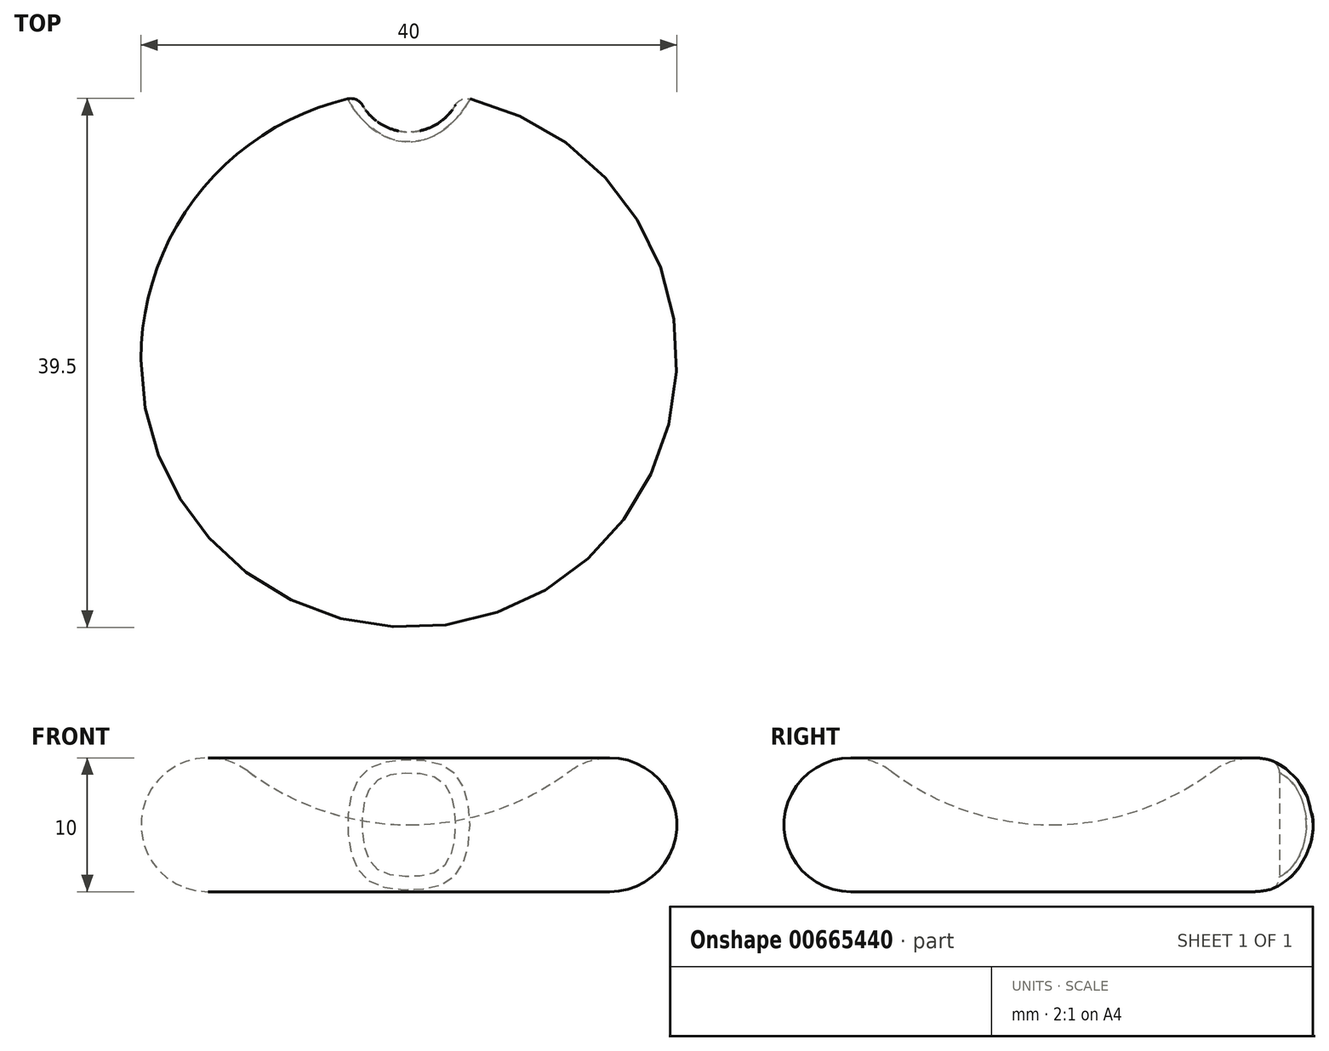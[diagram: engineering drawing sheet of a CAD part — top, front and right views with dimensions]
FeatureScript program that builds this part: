
annotation { "Feature Type Name" : "Feature", "Feature Type Description" : "" }
export const myFeature = defineFeature(function(context is Context, id is Id, definition is map)
    precondition{}
    {
        {
            var Q0;
            Q0=qCreatedBy(makeId("Front.planeOp"),FACE);
            var sketch = newSketch(context, id + "F0", { "sketchPlane" : qUnion([Q0])});
            skArc(sketch, "E0", {"start": v(-12, 9) * mm, "mid": v(-6.32, 6.03) * mm, "end": v(0, 5) * mm});
            skArc(sketch, "E1", {"start": v(-12, 9) * mm, "mid": v(-19.74, 6.58) * mm, "end": v(-15, 0) * mm});
            skLineSegment(sketch, "E2", {"start": v(0, 0) * mm, "end": v(-15, 0) * mm});
            skLineSegment(sketch, "E3", {"start": v(0, 0) * mm, "end": v(0, 5) * mm});
            skSolve(sketch);
        }
        {
            var Q0;
            Q0=makeQuery(id+"F0.imprint","IMPRINT",FACE,{"disambiguationData":[TD([[makeQuery(id+"F0.imprint","IMPRINT",EDGE,{"derivedFrom":sQuery(id+"F0.wireOp",EDGE,"E0")}),-1.0]])]});
            var Q1;
            Q1=sQuery(id+"F0.wireOp",EDGE,"E3");
            revolve(context, id + "F1", {"entities" : qUnion([Q0]), "axis" : qUnion([Q1]), "revolveType" : RevolveType.FULL});
        }
        {
            var Q0;
            Q0=qCreatedBy(makeId("Top.planeOp"),FACE);
            var sketch = newSketch(context, id + "F2", { "sketchPlane" : qUnion([Q0])});
            skCircle(sketch, "E4", {"center": v(0, 21) * mm, "radius": 4 * mm});
            skSolve(sketch);
        }
        {
            var Q0;
            Q0=qSketchRegion(id+"F2",true);
            extrude(context, id + "F3", {"entities" : qUnion([Q0]), "operationType" : NewBodyOperationType.REMOVE, "depth" : 13.9 * mm, "offsetDistance" : 25 * mm});
        }
        {
            var Q0;
            Q0=makeQuery(id+"F3.boolean.opBoolean","INTERSECT",EDGE,{"derivedFrom":[makeQuery(id+"F1.opRevolve","SWEPT_FACE",FACE,{"disambiguationData":[OSD([sQuery(id+"F0.wireOp",EDGE,"E1")])]}),makeQuery(id+"F3.opExtrude","SWEPT_FACE",FACE,{"disambiguationData":[OSD([sQuery(id+"F2.wireOp",EDGE,"E4")])]})]});
            fillet(context, id + "F4", {"entities" : qUnion([Q0]), "radius" : 1 * mm, "tangentPropagation" : true, "allowEdgeOverflow" : false});
        }
    });
